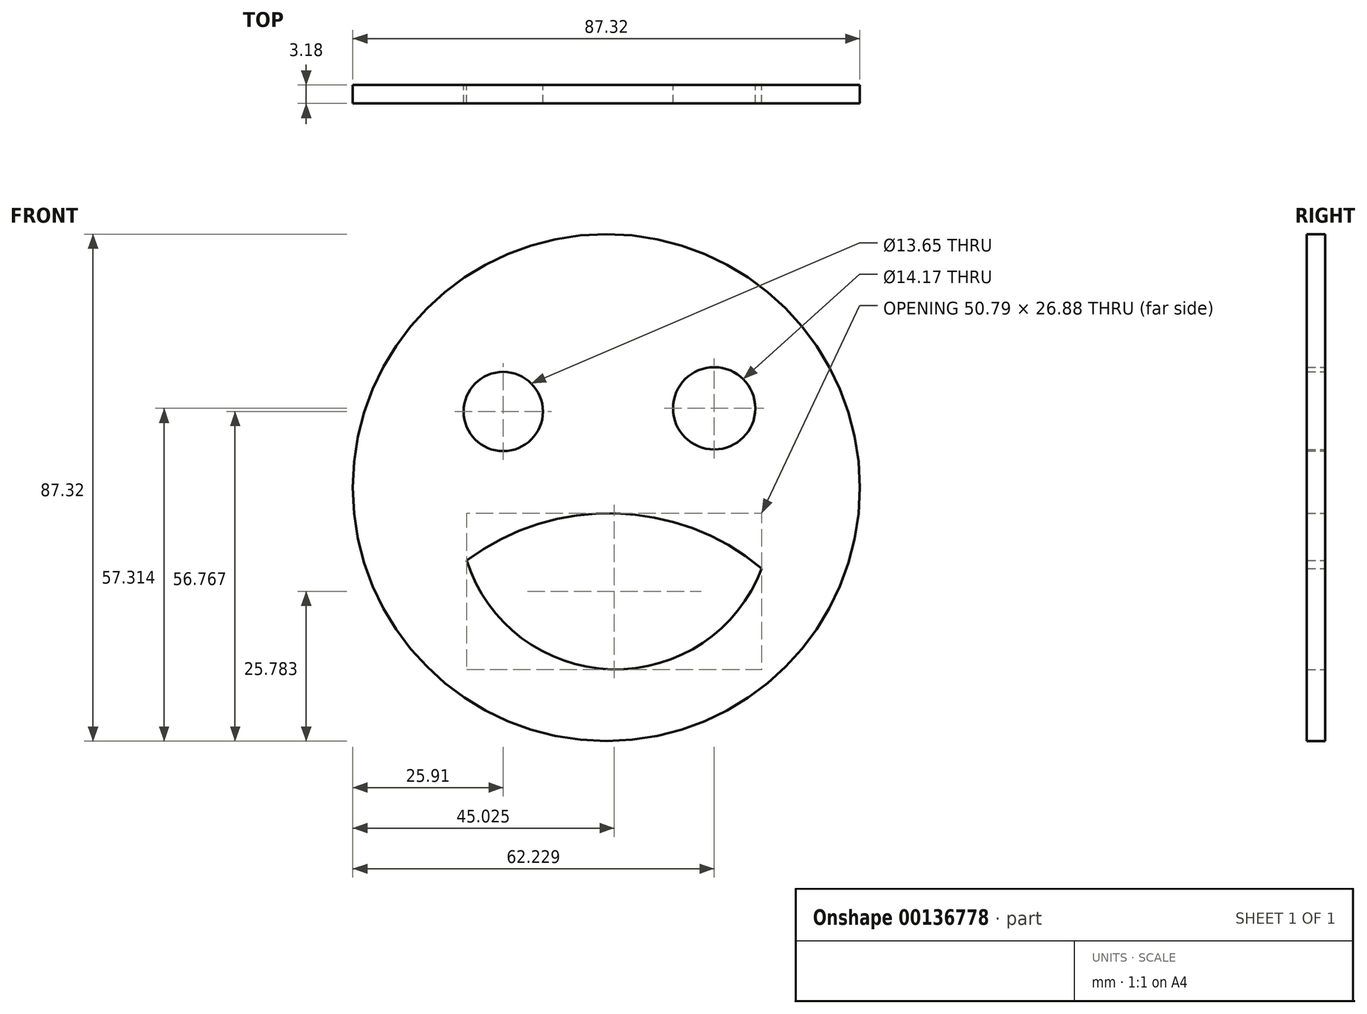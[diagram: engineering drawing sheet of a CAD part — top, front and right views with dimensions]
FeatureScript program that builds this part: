
annotation { "Feature Type Name" : "Feature", "Feature Type Description" : "" }
export const myFeature = defineFeature(function(context is Context, id is Id, definition is map)
    precondition{}
    {
        {
            var Q0;
            Q0=qCreatedBy(makeId("Front.planeOp"),FACE);
            var sketch = newSketch(context, id + "F0", { "sketchPlane" : qUnion([Q0])});
            skCircle(sketch, "E0", {"center": v(0, 0) * mm, "radius": 43.66 * mm});
            skCircle(sketch, "E1", {"center": v(-17.75, 13.1) * mm, "radius": 6.83 * mm});
            skCircle(sketch, "E2", {"center": v(18.57, 13.65) * mm, "radius": 7.08 * mm});
            skArc(sketch, "E3", {"start": v(-24.03, -12.56) * mm, "mid": v(0.88, -31.32) * mm, "end": v(26.76, -13.93) * mm});
            skArc(sketch, "E4", {"start": v(26.76, -13.93) * mm, "mid": v(1.6, -4.44) * mm, "end": v(-24.03, -12.56) * mm});
            skSolve(sketch);
        }
        {
            var Q0;
            Q0=makeQuery(id+"F0.imprint","IMPRINT",FACE,{"disambiguationData":[TD([[makeQuery(id+"F0.imprint","IMPRINT",EDGE,{"derivedFrom":sQuery(id+"F0.wireOp",EDGE,"E0")}),1.0]])]});
            extrude(context, id + "F1", {"entities" : qUnion([Q0]), "depth" : 3.17 * mm});
        }
    });
